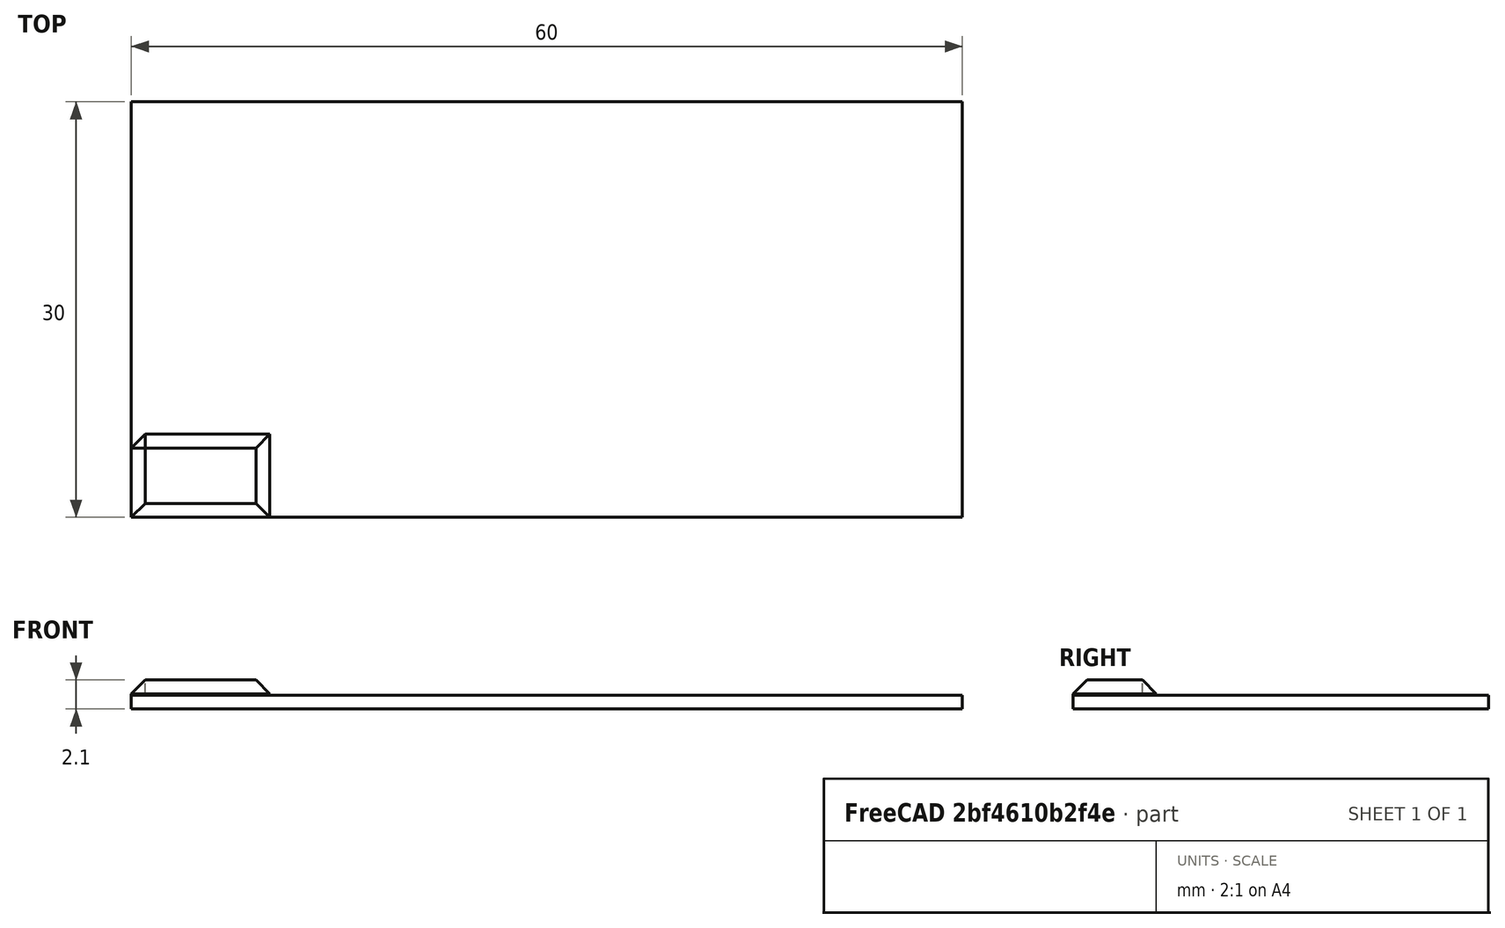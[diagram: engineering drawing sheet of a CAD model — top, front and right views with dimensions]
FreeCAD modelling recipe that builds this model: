
FCSTD DOCUMENT  (FreeCAD 0.21R33694 (Git))
Label: OJT1_T12P01_xocolata
License: All rights reserved
LicenseURL: http://en.wikipedia.org/wiki/All_rights_reserved
objects: Part::Box×2, Part::Chamfer×1, Part::FeaturePython×1
note: 3 computed .brp shape members not serialized (recipe doc carries the construction recipe); baked Part::Feature solids carry a one-line shape summary decoded from their .brp

FEATURE [Part::Box] Box  label="base"
  AttacherType = Attacher::AttachEngine3D
  Height = 1
  Length = 60
  Width = 30
FEATURE [Part::Box] Box001  label="Cube"
  AttacherType = Attacher::AttachEngine3D
  Height = 1.1
  Length = 10
  Placement = pos=(0,0,1) rot=(0,0,1;0rad)
  Width = 6
FEATURE [Part::Chamfer] Chamfer
  Base = -> Box001
  Edges = 5 edges r=1: [Edge2,Edge3,Edge6,Edge10,Edge12]
FEATURE [Part::FeaturePython] Array  # Draft array (typed FeaturePython)
  AlwaysSyncPlacement = false
  Angle = 360
  ArrayType = 0
  Axis = (0,0,1)
  Base = -> Chamfer
  Center = (0,0,0)
  Count = 30
  ExpandArray = false
  Fuse = false
  IntervalAxis = (0,0,0)
  IntervalX = (10,0,0)
  IntervalY = (0,6,0)
  IntervalZ = (0,0,100)
  NumberCircles = 3
  NumberPolar = 5
  NumberX = 6
  NumberY = 5
  NumberZ = 1
  PlacementList = 30 placements: [(0,0,0),(0,6,0),(0,12,0),(0,18,0),(0,24,0),(10,0,0),(10,6,0),(10,12,0),(10,18,0),(10,24,0),(20,0,0),(20,6,0),(20,12,0),(20,18,0),(20,24,0),(30,0,0),(30,6,0),(30,12,0),(30,18,0),(30,24,0),(40,0,0),(40,6,0),(40,12,0),(40,18,0),(40,24,0),(50,0,0),(50,6,0),(50,12,0),(50,18,0),(50,24,0)]
  RadialDistance = 50
  ScaleList = (30) [(1,1,1),(1,1,1),(1,1,1),(1,1,1),(1,1,1),(1,1,1),(1,1,1),(1,1,1),(1,1,1),(1,1,1),(1,1,1),(1,1,1),(1,1,1),(1,1,1),(1,1,1),(1,1,1),(1,1,1),(1,1,1),+12 more]
  Symmetry = 1
  TangentialDistance = 25
